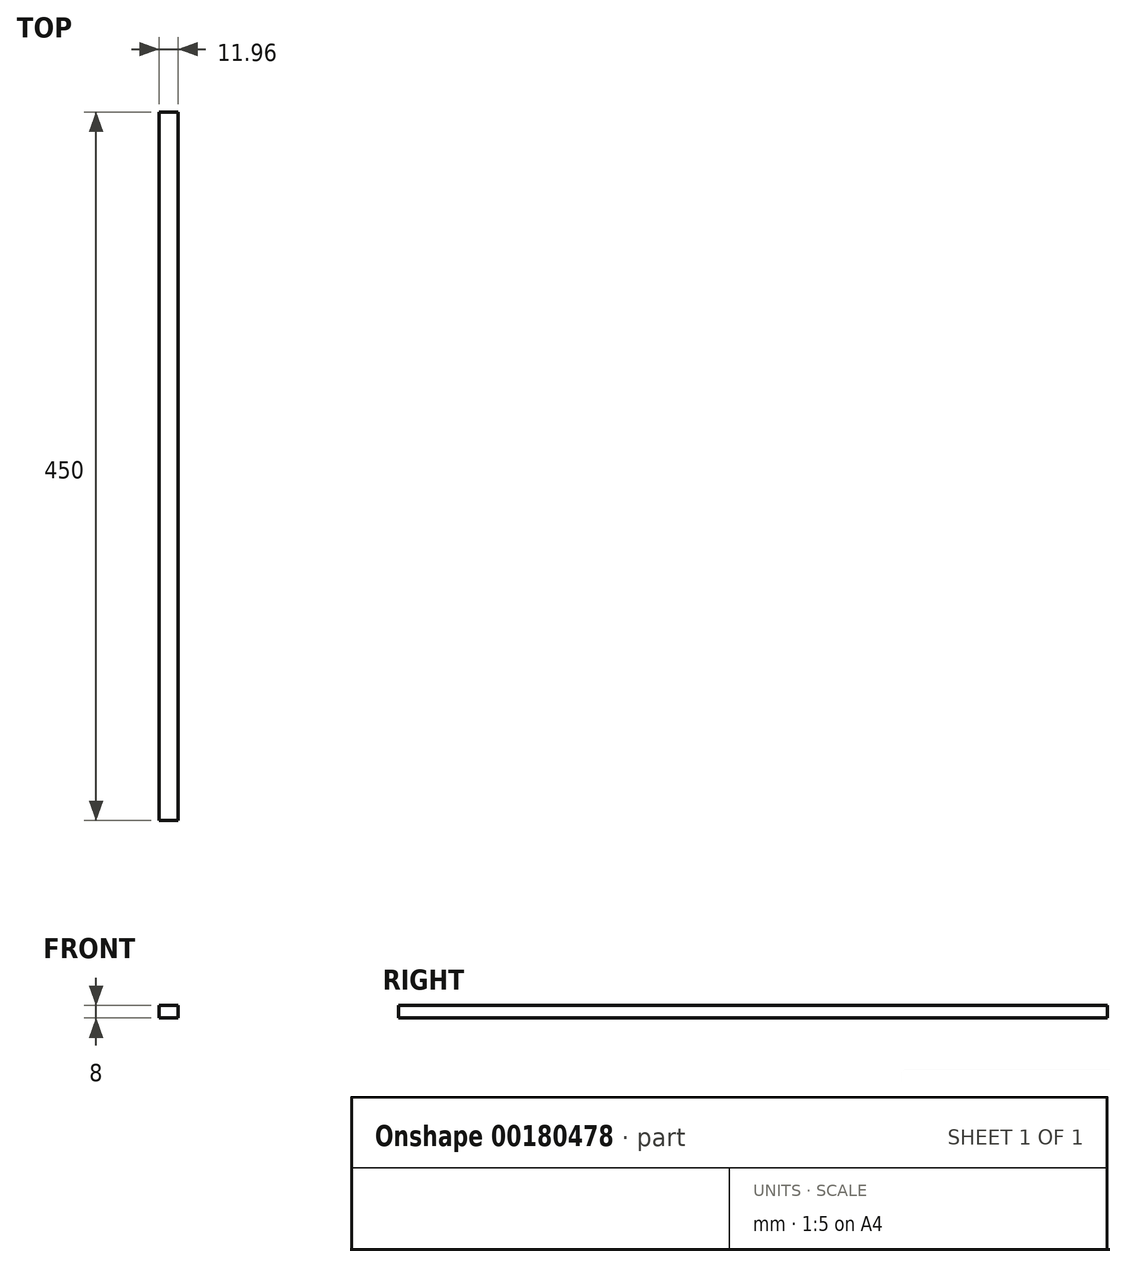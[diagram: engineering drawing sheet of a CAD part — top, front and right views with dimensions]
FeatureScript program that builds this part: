
annotation { "Feature Type Name" : "Feature", "Feature Type Description" : "" }
export const myFeature = defineFeature(function(context is Context, id is Id, definition is map)
    precondition{}
    {
        {
            var Q0;
            Q0=qCreatedBy(makeId("Front.planeOp"),FACE);
            var sketch = newSketch(context, id + "F0", { "sketchPlane" : qUnion([Q0])});
            skLineSegment(sketch, "E0.bottom", {"start": v(0, 8) * mm, "end": v(11.96, 8) * mm});
            skLineSegment(sketch, "E0.top", {"start": v(0, 0) * mm, "end": v(11.96, 0) * mm});
            skLineSegment(sketch, "E0.left", {"start": v(0, 8) * mm, "end": v(0, 0) * mm});
            skLineSegment(sketch, "E0.right", {"start": v(11.96, 8) * mm, "end": v(11.96, 0) * mm});
            skSolve(sketch);
        }
        {
            var Q0;
            Q0=makeQuery(id+"F0.imprint","IMPRINT",FACE,{"disambiguationData":[TD([[makeQuery(id+"F0.imprint","IMPRINT",EDGE,{"derivedFrom":sQuery(id+"F0.wireOp",EDGE,"E0.bottom")}),-1.0]])]});
            extrude(context, id + "F1", {"entities" : qUnion([Q0]), "depth" : 450 * mm});
        }
    });
